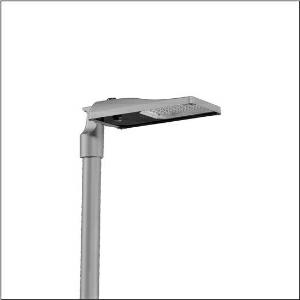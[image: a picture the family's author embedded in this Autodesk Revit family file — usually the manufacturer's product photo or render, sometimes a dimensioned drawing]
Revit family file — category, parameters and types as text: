
# Revit family: streetlight_sl_31_mini___st0_8a_5xh6c31t08ga_5d86
name_source: partatom
category: Lighting Fixtures
units: mm (PartAtom-declared; Revit-internal decimal feet)

## family parameters
Cut with Voids When Loaded = No
Host = Face
Light Source = No
Part Type = Normal
Room Calculation Point = No
Round Connector Dimension = Use Diameter
Shared = No

## types (1)
- --- (1 x LED, 5880 lm, 39.3 W, 3000K)
    Apparent Load = 39 VA
    CIE Flux Codes = 38 75 97 100 100
    Color Rendering = 70
    Color Temperature = 3000K
    Default Elevation = 1800 mm
    Description = Streetlight SL 31 mini D4i, Desk-Remote mast luminaire for post-top, side-entry; light control with lens of PMMA; light distribution: ST0.8a, direct asymmetric distribution, for standard-compliant lighting for roads and squares; LED: luminous flux: 5.880lm, light colour: 730, colour temperature: 3000K; luminous efficacy: 149,6lm/W; control: pre-setting: logarithmic dimming characteristic, flexible luminous flux parameterisation, time-dependent luminous flux control, constant luminous flux control, power reduction, intelligent temperature release in ECG and LED module, overheat protection; luminaire housing, of diecast aluminium, Siteco® metallic grey (DB 702S), corrosivity category C5 high according to DIN EN ISO 12944; cover of toughened safety glass, transparent, opened without tools; mast flange of diecast aluminium, Siteco® metallic grey (DB 702S), spigot size: 76/60mm, mast flange included unmounted; with cable H07RN-F 2x 1.5mm², cable length: 6,5m, connection cable pre-assembled; mains connection: 220..240V, AC, 50/60Hz; power consumption (at start of service life): 39,3W / (at end of service life): 40,7W / (with reduced operation 50%): 18,1W; protection rating (complete): IP66; insulation class (complete): insulation class II (safety insulation); impact resistance: IK09; certification: CE, ENEC, ENEC+, VDE, UKCA, ZD4i; permissible operating ambient temperature for outdoor applications: -40..+50°C; packaging unit: 1 piece

Light Distribution: ST0.8a
    Height = 76 mm
    Lamp = 1 x LED
    Lamp Light Flux = 5880 lm
    Lamp Power = 39.3 W
    Lamp count = 1
    Length = 547 mm
    Luminous efficacy = 150 lm/W
    Manufacturer = Siteco
    ModVariant = No
    Model = 5XH6C31T08GA
    Number of Poles = 1
    OnlyDefault = Yes
    Power Factor = 1
    Product Name = Streetlight SL 31 mini | ST0.8a
    Product group = mast luminaire | pylon top
    ProductGroupID = 6100
    Protection Class = Protection class II
    Protection Degree = IP 66
    RLX_Detail_Level = 1
    RLX_Emergency_Light_Flux = 0 lm
    RLX_Emergency_Type = 0
    RLX_Emergency_Type_DB = No
    RlxData = <blob elided: 39809 chars, md5=17fd06bc>
    Socket = socket
    Standby Power = 0 W
    System Light Flux = 5880 lm
    System Power = 39 W
    Type Comments = factory setting: luminous flux: 100 % | dim-lin: 254 | 798 mA
    Type Image = l_1300332.jpg
    URL = http://relux.com
    VarID = @adj_070251
    Voltage = 0 V
    Weight = 0.00 kg
    Width = 265 mm

## geometry (parser evidence)
native form markers: Blend x4, Sweep x9
no freeform markers — native parametric forms only
